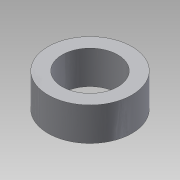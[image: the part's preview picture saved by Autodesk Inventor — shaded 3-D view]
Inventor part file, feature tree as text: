
AUTODESK INVENTOR PART (.ipt)
format: ipt  version: 2013 SP2 (Build 170200200, 200)  size: 81,920 bytes
history: native  units: mm
features: extrude x1, sketch x1
ambient origin geometry x8: Origin, YZ Plane, XZ Plane, XY Plane, X Axis, Y Axis, Z Axis, Center Point
bodies: Solid1 (feature_tree)
feature tree (2):
  extrude  "Extrusion1"  Depth=8.0mm
  sketch  "Sketch1"  dims[d0=5.3mm d1=8.0mm d3=0.0mm]
